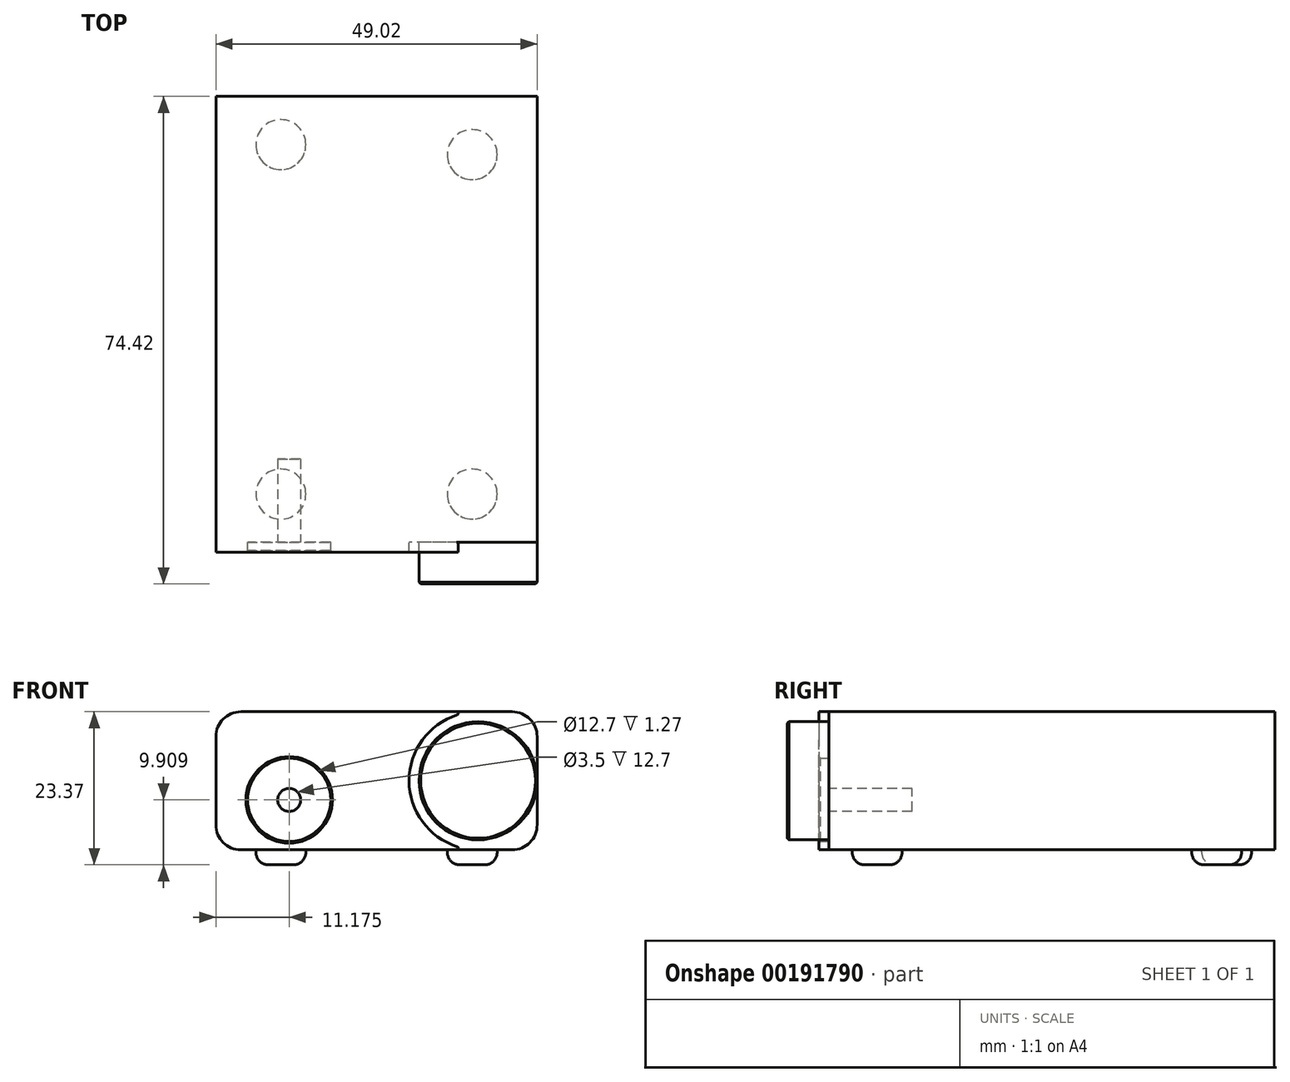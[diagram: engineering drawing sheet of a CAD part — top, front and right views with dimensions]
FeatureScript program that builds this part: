
annotation { "Feature Type Name" : "Feature", "Feature Type Description" : "" }
export const myFeature = defineFeature(function(context is Context, id is Id, definition is map)
    precondition{}
    {
        {
            var Q0;
            Q0=qCreatedBy(makeId("Front.planeOp"),FACE);
            var sketch = newSketch(context, id + "F0", { "sketchPlane" : qUnion([Q0])});
            skLineSegment(sketch, "E0.bottom", {"start": v(20.7, -10.54) * mm, "end": v(-20.7, -10.54) * mm});
            skLineSegment(sketch, "E0.top", {"start": v(20.7, 10.54) * mm, "end": v(-20.7, 10.54) * mm});
            skLineSegment(sketch, "E0.left", {"start": v(24.51, -6.73) * mm, "end": v(24.51, 6.73) * mm});
            skLineSegment(sketch, "E0.right", {"start": v(-24.51, -6.73) * mm, "end": v(-24.51, 6.73) * mm});
            skPoint(sketch, "E0.middle", {"position": v(0, 0) * mm});
            skPoint(sketch, "E1.visualSharp", {"position": v(-24.51, 10.54) * mm});
            skArc(sketch, "E1.filletArc", {"start": v(-20.7, 10.54) * mm, "mid": v(-23.4, 9.43) * mm, "end": v(-24.51, 6.73) * mm});
            skPoint(sketch, "E2.visualSharp", {"position": v(-24.51, -10.54) * mm});
            skArc(sketch, "E2.filletArc", {"start": v(-24.51, -6.73) * mm, "mid": v(-23.4, -9.43) * mm, "end": v(-20.7, -10.54) * mm});
            skPoint(sketch, "E3.visualSharp", {"position": v(24.51, -10.54) * mm});
            skArc(sketch, "E3.filletArc", {"start": v(20.7, -10.54) * mm, "mid": v(23.4, -9.43) * mm, "end": v(24.51, -6.73) * mm});
            skPoint(sketch, "E4.visualSharp", {"position": v(24.51, 10.54) * mm});
            skArc(sketch, "E4.filletArc", {"start": v(24.51, 6.73) * mm, "mid": v(23.4, 9.43) * mm, "end": v(20.7, 10.54) * mm});
            skCircle(sketch, "E5", {"center": v(15.5, 0) * mm, "radius": 9.02 * mm});
            skArc(sketch, "E6", {"start": v(15.5, 10.54) * mm, "mid": v(4.95, 0) * mm, "end": v(15.5, -10.54) * mm});
            skCircle(sketch, "E7", {"center": v(-13.33, -2.92) * mm, "radius": 1.75 * mm});
            skCircle(sketch, "E8", {"center": v(-13.33, -2.92) * mm, "radius": 6.35 * mm});
            skSolve(sketch);
        }
        {
            var Q0;
            Q0=makeQuery(id+"F0.imprint","IMPRINT",FACE,{"disambiguationData":[TD([[makeQuery(id+"F0.imprint","IMPRINT",EDGE,{"derivedFrom":sQuery(id+"F0.wireOp",EDGE,"E0.right")}),-1.0]])]});
            var Q1;
            Q1=makeQuery(id+"F0.imprint","IMPRINT",FACE,{"disambiguationData":[TD([[makeQuery(id+"F0.imprint","IMPRINT",EDGE,{"derivedFrom":sQuery(id+"F0.wireOp",EDGE,"E7")}),-1.0]])]});
            var Q2;
            Q2=makeQuery(id+"F0.imprint","IMPRINT",FACE,{"disambiguationData":[TD([[makeQuery(id+"F0.imprint","IMPRINT",EDGE,{"derivedFrom":sQuery(id+"F0.wireOp",EDGE,"E7")}),1.0]])]});
            var Q3;
            Q3=makeQuery(id+"F0.imprint","IMPRINT",FACE,{"disambiguationData":[TD([[makeQuery(id+"F0.imprint","IMPRINT",EDGE,{"derivedFrom":sQuery(id+"F0.wireOp",EDGE,"E5")}),1.0]])]});
            var Q4;
            {var subQ5=sQuery(id+"F0.wireOp",EDGE,"E3.filletArc");Q4=makeQuery(id+"F0.imprint","IMPRINT",FACE,{"disambiguationData":[TD([[makeQuery(id+"F0.imprint","IMPRINT",EDGE,{"derivedFrom":subQ5}),1.0]])]});}
            extrude(context, id + "F1", {"entities" : qUnion([Q0, Q1, Q2, Q3, Q4]), "oppositeDirection" : true, "depth" : 68.07 * mm});
        }
        {
            var Q0;
            Q0=makeQuery(id+"F0.imprint","IMPRINT",FACE,{"disambiguationData":[TD([[makeQuery(id+"F0.imprint","IMPRINT",EDGE,{"derivedFrom":sQuery(id+"F0.wireOp",EDGE,"E5")}),1.0]])]});
            extrude(context, id + "F2", {"entities" : qUnion([Q0]), "operationType" : NewBodyOperationType.ADD, "depth" : 6.35 * mm});
        }
        {
            var Q0;
            Q0=makeQuery(id+"F0.imprint","IMPRINT",FACE,{"disambiguationData":[TD([[makeQuery(id+"F0.imprint","IMPRINT",EDGE,{"derivedFrom":sQuery(id+"F0.wireOp",EDGE,"E0.right")}),-1.0]])]});
            extrude(context, id + "F3", {"entities" : qUnion([Q0]), "operationType" : NewBodyOperationType.ADD, "depth" : 1.52 * mm});
        }
        {
            var Q0;
            Q0=makeQuery(id+"F0.imprint","IMPRINT",FACE,{"disambiguationData":[TD([[makeQuery(id+"F0.imprint","IMPRINT",EDGE,{"derivedFrom":sQuery(id+"F0.wireOp",EDGE,"E7")}),1.0]])]});
            extrude(context, id + "F4", {"entities" : qUnion([Q0]), "operationType" : NewBodyOperationType.REMOVE, "oppositeDirection" : true, "depth" : 12.7 * mm});
        }
        {
            var Q0;
            Q0=makeQuery(id+"F3.opExtrude","SWEPT_EDGE",EDGE,{"disambiguationData":[OSD([sQuery(id+"F0.wireOp",EDGE,"E0.top"),sQuery(id+"F0.wireOp",EDGE,"E6")])]});
            var Q1;
            Q1=makeQuery(id+"F3.opExtrude","SWEPT_EDGE",EDGE,{"disambiguationData":[OSD([sQuery(id+"F0.wireOp",EDGE,"E0.bottom"),sQuery(id+"F0.wireOp",EDGE,"E6")])]});
            fillet(context, id + "F5", {"entities" : qUnion([Q0, Q1]), "radius" : 0.25 * mm, "tangentPropagation" : true, "allowEdgeOverflow" : false});
        }
        {
            var Q0;
            Q0=makeQuery(id+"F2.opExtrude","CAP_EDGE",EDGE,{"disambiguationData":[OSD([sQuery(id+"F0.wireOp",EDGE,"E5")])],"isStart":false});
            var Q1;
            Q1=makeQuery(id+"F3.opExtrude","CAP_EDGE",EDGE,{"disambiguationData":[OSD([sQuery(id+"F0.wireOp",EDGE,"E8")])],"isStart":false});
            chamfer(context, id + "F6", {"entities" : qUnion([Q0, Q1]), "width" : 0.25 * mm, "tangentPropagation" : true});
        }
        {
            var Q0;
            {var subQ0=sQuery(id+"F0.wireOp",EDGE,"E0.bottom");Q0=makeQuery(id+"F3.boolean.opBoolean","MERGE",FACE,{"derivedFrom":[makeQuery(id+"F1.opExtrude","SWEPT_FACE",FACE,{"disambiguationData":[OSD([subQ0])]}),makeQuery(id+"F3.opExtrude","SWEPT_FACE",FACE,{"disambiguationData":[OSD([subQ0])]})]});}
            var sketch = newSketch(context, id + "F7", { "sketchPlane" : qUnion([Q0])});
            skCircle(sketch, "E9", {"center": v(-14.6, -7.37) * mm, "radius": 3.81 * mm});
            skCircle(sketch, "E10.MirrorC", {"center": v(14.6, -7.37) * mm, "radius": 3.81 * mm});
            skCircle(sketch, "E11.MirrorC", {"center": v(-14.6, -60.7) * mm, "radius": 3.81 * mm});
            skCircle(sketch, "E12.MirrorC", {"center": v(14.6, -59.18) * mm, "radius": 3.81 * mm});
            skSolve(sketch);
        }
        {
            var Q0;
            Q0 = qSketchRegion(id + "F7", true);
            extrude(context, id + "F8", {"entities" : qUnion([Q0]), "operationType" : NewBodyOperationType.ADD, "depth" : 2.3 * mm});
        }
        {
            var Q0;
            Q0=makeQuery(id+"F8.opExtrude","CAP_EDGE",EDGE,{"disambiguationData":[OSD([sQuery(id+"F7.wireOp",EDGE,"E9")])],"isStart":false});
            var Q1;
            Q1=makeQuery(id+"F8.opExtrude","CAP_EDGE",EDGE,{"disambiguationData":[OSD([sQuery(id+"F7.wireOp",EDGE,"E10.MirrorC")])],"isStart":false});
            var Q2;
            Q2=makeQuery(id+"F8.opExtrude","CAP_FACE",FACE,{"disambiguationData":[OSD([sQuery(id+"F7.wireOp",EDGE,"E12.MirrorC")])],"isStart":false});
            var Q3;
            Q3=makeQuery(id+"F8.opExtrude","CAP_EDGE",EDGE,{"disambiguationData":[OSD([sQuery(id+"F7.wireOp",EDGE,"E11.MirrorC")])],"isStart":false});
            fillet(context, id + "F9", {"entities" : qUnion([Q0, Q1, Q2, Q3]), "radius" : 1.9 * mm, "tangentPropagation" : true, "allowEdgeOverflow" : false});
        }
    });
